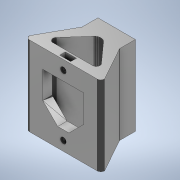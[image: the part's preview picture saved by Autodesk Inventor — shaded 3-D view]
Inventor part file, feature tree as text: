
AUTODESK INVENTOR PART (.ipt)
format: ipt  version: 2021 (Build 250183000, 183)  size: 1,984,512 bytes
history: native  units: in
note: dims shown in document units (in); Inventor stores cm internally (conversion verified against a paired STEP export)
features: other x3, plane x2, split x2, extrude x2, sketch x2, move_body x1, boolean_combine x1
ambient origin geometry x8: Origin, YZ Plane, XZ Plane, XY Plane, X Axis, Y Axis, Z Axis, Center Point
bodies: Solid1 (feature_tree), Solid2 (feature_tree), Solid3 (feature_tree)
feature tree (13):
  other  "PenSlider.ipt"
  plane  "Work Plane1"
  split  "Split1"
  plane  "Work Plane2"
  split  "Split2"
  move_body  "Move Body1"
  boolean_combine  "Combine1"
  extrude  "Extrusion3"  [1 undecoded]
  extrude  "Extrusion4"  Depth=0.3937in TaperAngle=0.0deg
  other  "Solid3::PenSlider.ipt"
  other  "TaggingFeature1"
  sketch  "Sketch4"  dims[d0=0.3937in d1=-0.709in]
  sketch  "Sketch5"  dims[d2=-1.125in d3=0.0in d4=0.416in d5=0.0in d16=0.1969in d17=0.3937in d18=0.0in d19=0.3937in d20=0.0in d21=0.1892in]
note: 1 required parameter value undecoded (feature->parameter linkage not recoverable at this tier; creation-order binding heuristic only, values carry confidence <= 0.55)
